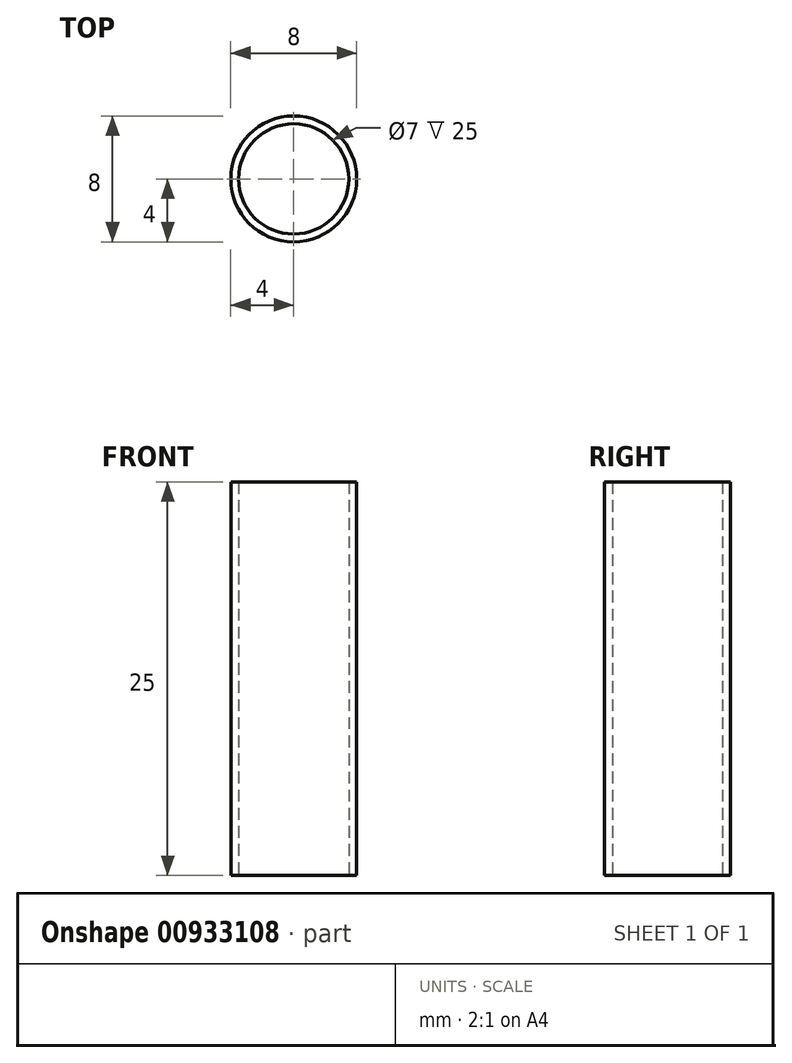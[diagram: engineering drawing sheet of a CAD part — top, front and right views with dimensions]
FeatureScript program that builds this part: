
annotation { "Feature Type Name" : "Feature", "Feature Type Description" : "" }
export const myFeature = defineFeature(function(context is Context, id is Id, definition is map)
    precondition{}
    {
        {
            var Q0;
            Q0=qCreatedBy(makeId("Top.planeOp"),FACE);
            var sketch = newSketch(context, id + "F0", { "sketchPlane" : qUnion([Q0])});
            skCircle(sketch, "E0", {"center": v(0, 0) * mm, "radius": 3.5 * mm});
            skCircle(sketch, "E1", {"center": v(0, 0) * mm, "radius": 4 * mm});
            skSolve(sketch);
        }
        {
            var Q0;
            Q0 = qSketchRegion(id + "F0", true);
            extrude(context, id + "F1", {"entities" : qUnion([Q0]), "depth" : 25 * mm, "offsetDistance" : 25 * mm});
        }
    });
